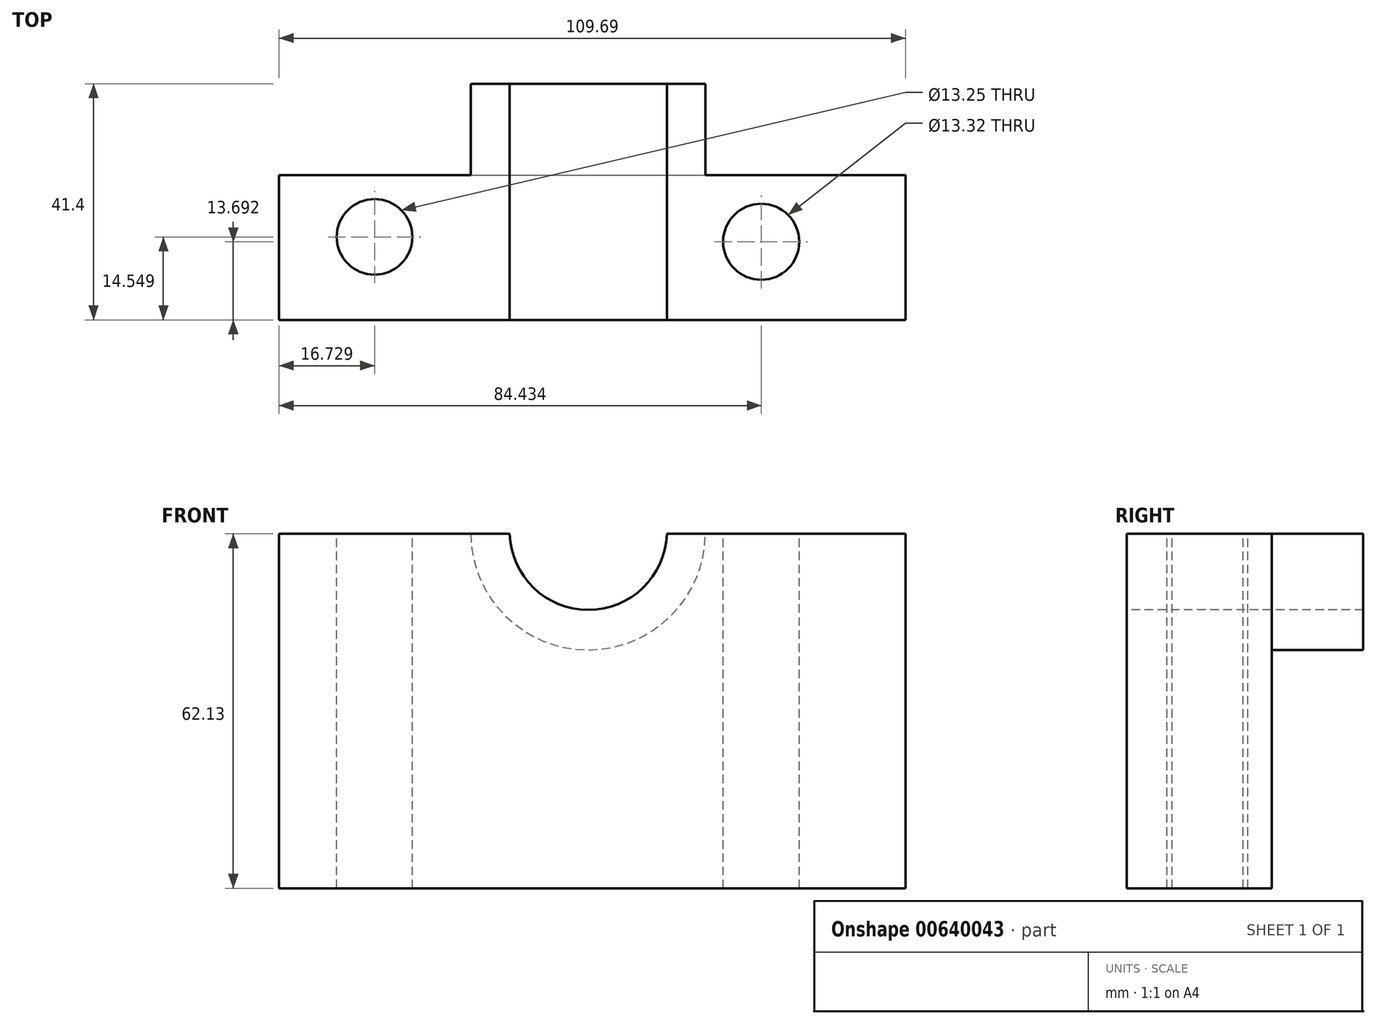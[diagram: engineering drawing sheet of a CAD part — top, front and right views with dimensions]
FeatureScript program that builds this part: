
annotation { "Feature Type Name" : "Feature", "Feature Type Description" : "" }
export const myFeature = defineFeature(function(context is Context, id is Id, definition is map)
    precondition{}
    {
        {
            var Q0;
            Q0=qCreatedBy(makeId("Front.planeOp"),FACE);
            var sketch = newSketch(context, id + "F0", { "sketchPlane" : qUnion([Q0])});
            skLineSegment(sketch, "E0", {"start": v(-51.34, 36.41) * mm, "end": v(-51.34, -25.72) * mm});
            skLineSegment(sketch, "E1", {"start": v(-51.34, -25.72) * mm, "end": v(58.35, -25.72) * mm});
            skLineSegment(sketch, "E2", {"start": v(58.35, -25.72) * mm, "end": v(58.35, 36.41) * mm});
            skLineSegment(sketch, "E3", {"start": v(58.35, 36.41) * mm, "end": v(23.32, 36.41) * mm});
            skLineSegment(sketch, "E4", {"start": v(-51.34, 36.41) * mm, "end": v(-17.8, 36.41) * mm});
            skArc(sketch, "E5", {"start": v(-17.8, 36.41) * mm, "mid": v(2.77, 16.06) * mm, "end": v(23.32, 36.41) * mm});
            skLineSegment(sketch, "E6", {"start": v(-17.8, 36.41) * mm, "end": v(-12.26, 36.41) * mm});
            skLineSegment(sketch, "E7", {"start": v(23.32, 36.41) * mm, "end": v(17.05, 36.41) * mm});
            skArc(sketch, "E8", {"start": v(-12.26, 36.41) * mm, "mid": v(2.4, 21.95) * mm, "end": v(17.05, 36.41) * mm});
            skSolve(sketch);
        }
        {
            var Q0;
            Q0=makeQuery(id+"F0.imprint","IMPRINT",FACE,{"disambiguationData":[TD([[makeQuery(id+"F0.imprint","IMPRINT",EDGE,{"derivedFrom":sQuery(id+"F0.wireOp",EDGE,"E0")}),1.0]])]});
            extrude(context, id + "F1", {"entities" : qUnion([Q0]), "depth" : 25.4 * mm, "offsetDistance" : 25.4 * mm});
        }
        {
            var Q0;
            Q0=makeQuery(id+"F1.opExtrude","CAP_FACE",FACE,{"disambiguationData":[OSD([sQuery(id+"F0.wireOp",EDGE,"E0"),sQuery(id+"F0.wireOp",EDGE,"E1"),sQuery(id+"F0.wireOp",EDGE,"E2"),sQuery(id+"F0.wireOp",EDGE,"E3"),sQuery(id+"F0.wireOp",EDGE,"E4"),sQuery(id+"F0.wireOp",EDGE,"E5")])],"isStart":false});
            var sketch = newSketch(context, id + "F2", { "sketchPlane" : qUnion([Q0])});
            skLineSegment(sketch, "E9", {"start": v(-17.8, 36.41) * mm, "end": v(-10.93, 36.41) * mm});
            skLineSegment(sketch, "E10", {"start": v(23.32, 36.41) * mm, "end": v(16.57, 36.41) * mm});
            skArc(sketch, "E11", {"start": v(-10.93, 36.41) * mm, "mid": v(2.82, 23.07) * mm, "end": v(16.57, 36.41) * mm});
            skSolve(sketch);
        }
        {
            var Q0;
            Q0=makeQuery(id+"F2.imprint","IMPRINT",FACE,{"disambiguationData":[TD([[makeQuery(id+"F2.imprint","IMPRINT",EDGE,{"derivedFrom":sQuery(id+"F2.wireOp",EDGE,"E9")}),-1.0]])]});
            extrude(context, id + "F3", {"entities" : qUnion([Q0]), "operationType" : NewBodyOperationType.ADD, "oppositeDirection" : true, "depth" : 41.4 * mm, "offsetDistance" : 25.4 * mm});
        }
        {
            var Q0;
            Q0=makeQuery(id+"F3.boolean.opBoolean","MERGE",FACE,{"derivedFrom":[makeQuery(id+"F1.opExtrude","SWEPT_FACE",FACE,{"disambiguationData":[OSD([sQuery(id+"F0.wireOp",EDGE,"E3")])]}),makeQuery(id+"F3.opExtrude","SWEPT_FACE",FACE,{"disambiguationData":[OSD([sQuery(id+"F2.wireOp",EDGE,"E10")])]})]});
            var sketch = newSketch(context, id + "F4", { "sketchPlane" : qUnion([Q0])});
            skCircle(sketch, "E12", {"center": v(-34.61, -10.85) * mm, "radius": 6.63 * mm});
            skSolve(sketch);
        }
        {
            var Q0;
            {var subQ1=sQuery(id+"F0.wireOp",EDGE,"E3");Q0=makeQuery(id+"F4.imprint","IMPRINT",FACE,{"disambiguationData":[TD([[makeQuery(id+"F4.imprint","IMPRINT",EDGE,{"derivedFrom":makeQuery(id+"F1.opExtrude","CAP_EDGE",EDGE,{"disambiguationData":[OSD([subQ1])],"isStart":true})}),1.0]])]});}
            var sketch = newSketch(context, id + "F5", { "sketchPlane" : qUnion([Q0])});
            skCircle(sketch, "E13", {"center": v(33.1, -11.7) * mm, "radius": 6.66 * mm});
            skSolve(sketch);
        }
        {
            var Q0;
            Q0=makeQuery(id+"F4.imprint","IMPRINT",FACE,{"disambiguationData":[TD([[makeQuery(id+"F4.imprint","IMPRINT",EDGE,{"derivedFrom":sQuery(id+"F4.wireOp",EDGE,"E12")}),1.0]])]});
            extrude(context, id + "F6", {"entities" : qUnion([Q0]), "operationType" : NewBodyOperationType.REMOVE, "oppositeDirection" : true, "depth" : 212.6 * mm, "offsetDistance" : 25.4 * mm});
        }
        {
            var Q0;
            Q0=makeQuery(id+"F5.imprint","IMPRINT",FACE,{"disambiguationData":[TD([[makeQuery(id+"F5.imprint","IMPRINT",EDGE,{"derivedFrom":sQuery(id+"F5.wireOp",EDGE,"E13")}),1.0]])]});
            extrude(context, id + "F7", {"entities" : qUnion([Q0]), "operationType" : NewBodyOperationType.REMOVE, "oppositeDirection" : true, "depth" : 146.05 * mm, "offsetDistance" : 25.4 * mm});
        }
    });
